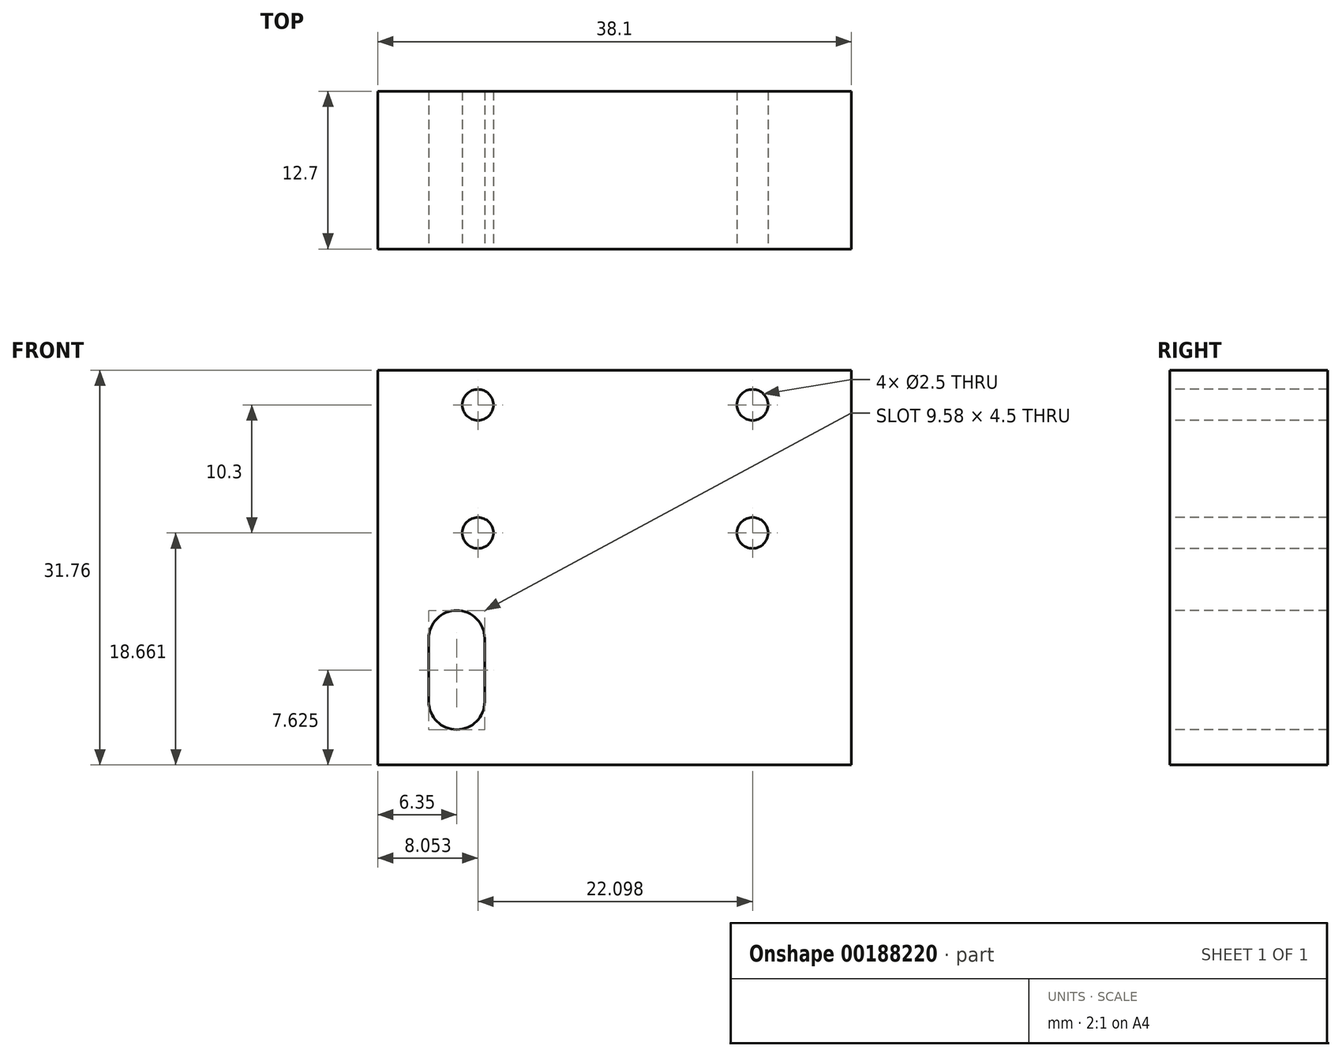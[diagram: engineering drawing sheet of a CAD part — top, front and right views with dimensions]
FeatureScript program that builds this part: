
annotation { "Feature Type Name" : "Feature", "Feature Type Description" : "" }
export const myFeature = defineFeature(function(context is Context, id is Id, definition is map)
    precondition{}
    {
        {
            var Q0;
            Q0=qCreatedBy(makeId("Front.planeOp"),FACE);
            var sketch = newSketch(context, id + "F0", { "sketchPlane" : qUnion([Q0])});
            skLineSegment(sketch, "E0.bottom", {"start": v(19.05, -15.88) * mm, "end": v(-19.05, -15.88) * mm});
            skLineSegment(sketch, "E0.top", {"start": v(19.05, 15.88) * mm, "end": v(-19.05, 15.87) * mm});
            skLineSegment(sketch, "E0.left", {"start": v(19.05, -15.88) * mm, "end": v(19.05, 15.88) * mm});
            skLineSegment(sketch, "E0.right", {"start": v(-19.05, -15.88) * mm, "end": v(-19.05, 15.87) * mm});
            skPoint(sketch, "E0.middle", {"position": v(0, 0) * mm});
            skSolve(sketch);
        }
        {
            var Q0;
            Q0 = qSketchRegion(id + "F0", true);
            extrude(context, id + "F1", {"entities" : qUnion([Q0]), "endBound" : BoundingType.SYMMETRIC, "depth" : 12.7 * mm});
        }
        {
            var Q0;
            Q0=makeQuery(id+"F1.opExtrude","CAP_FACE",FACE,{"disambiguationData":[OSD([sQuery(id+"F0.wireOp",EDGE,"E0.bottom"),sQuery(id+"F0.wireOp",EDGE,"E0.top"),sQuery(id+"F0.wireOp",EDGE,"E0.left"),sQuery(id+"F0.wireOp",EDGE,"E0.right")])],"isStart":false});
            var sketch = newSketch(context, id + "F2", { "sketchPlane" : qUnion([Q0])});
            skPoint(sketch, "E1", {"position": v(11.1, 13.08) * mm});
            skPoint(sketch, "E2", {"position": v(-11, 2.78) * mm});
            skPoint(sketch, "E3", {"position": v(-11, 13.08) * mm});
            skPoint(sketch, "E4", {"position": v(11.1, 2.78) * mm});
            skSolve(sketch);
        }
        {
            var Q0;
            Q0=sQuery(id+"F2.wireOp",VERTEX,"E2");
            var Q1;
            Q1=sQuery(id+"F2.wireOp",VERTEX,"E1");
            var Q2;
            Q2=sQuery(id+"F2.wireOp",VERTEX,"E3");
            var Q3;
            Q3=sQuery(id+"F2.wireOp",VERTEX,"E4");
            var Q4;
            Q4=makeQuery(id+"F1.opExtrude","SWEPT_BODY",BODY,{"disambiguationData":[OSD([sQuery(id+"F0.wireOp",EDGE,"E0.bottom"),sQuery(id+"F0.wireOp",EDGE,"E0.top"),sQuery(id+"F0.wireOp",EDGE,"E0.left"),sQuery(id+"F0.wireOp",EDGE,"E0.right")])]});
            hole(context, id + "F3", {"style" : HoleStyle.SIMPLE, "endStyle" : HoleEndStyle.THROUGH, "standardTappedOrClearance" : lookupTablePath({ "standard" : "ISO", "engagement" : "75%", "pitch" : "0.5 mm", "size" : "M3", "type" : "Tapped" }), "standardBlindInLast" : lookupTablePath({ "standard" : "ISO", "engagement" : "75%", "pitch" : "0.5 mm", "size" : "M3", "type" : "Tapped" }), "holeDiameter" : 2.5 * mm, "locations" : qUnion([Q0, Q1, Q2, Q3]), "scope" : qUnion([Q4]), "isTappedThrough" : true, "majorDiameter" : 3 * mm, "showTappedDepth" : true});
        }
        {
            var Q0;
            Q0=makeQuery(id+"F1.opExtrude","CAP_FACE",FACE,{"disambiguationData":[OSD([sQuery(id+"F0.wireOp",EDGE,"E0.bottom"),sQuery(id+"F0.wireOp",EDGE,"E0.top"),sQuery(id+"F0.wireOp",EDGE,"E0.left"),sQuery(id+"F0.wireOp",EDGE,"E0.right")])],"isStart":false});
            var sketch = newSketch(context, id + "F4", { "sketchPlane" : qUnion([Q0])});
            skLineSegment(sketch, "E5", {"start": v(-12.7, -5.72) * mm, "end": v(-12.7, -10.8) * mm});
            skArc(sketch, "E6.0.startCap", {"start": v(-14.95, -5.72) * mm, "mid": v(-12.7, -3.47) * mm, "end": v(-10.45, -5.72) * mm});
            skArc(sketch, "E6.0.endCap", {"start": v(-10.45, -10.8) * mm, "mid": v(-12.7, -13.05) * mm, "end": v(-14.95, -10.8) * mm});
            skLineSegment(sketch, "E6.0.left", {"start": v(-10.45, -5.72) * mm, "end": v(-10.45, -10.8) * mm});
            skLineSegment(sketch, "E6.0.right", {"start": v(-14.95, -5.72) * mm, "end": v(-14.95, -10.8) * mm});
            skSolve(sketch);
        }
        {
            var Q0;
            Q0 = qSketchRegion(id + "F4", true);
            extrude(context, id + "F5", {"entities" : qUnion([Q0]), "operationType" : NewBodyOperationType.REMOVE, "endBound" : BoundingType.UP_TO_NEXT, "oppositeDirection" : true, "depth" : 25.4 * mm});
        }
    });
